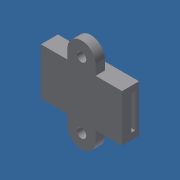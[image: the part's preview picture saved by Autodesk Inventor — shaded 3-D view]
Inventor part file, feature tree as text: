
AUTODESK INVENTOR PART (.ipt)
format: ipt  version: 2021 (Build 250183000, 183)  size: 143,360 bytes
history: native  units: mm
features: extrude x3, sketch x3
ambient origin geometry x8: Origin, YZ Plane, XZ Plane, XY Plane, X Axis, Y Axis, Z Axis, Center Point
bodies: Solid1 (feature_tree)
feature tree (6):
  extrude  "Extrusion1"  Depth=25.0mm
  extrude  "Extrusion2"  Depth=15.0mm
  extrude  "Extrusion3"  Depth=21.5mm
  sketch  "Sketch1"  dims[d0=43.0mm d1=25.0mm]
  sketch  "Sketch2"  dims[d2=15.0mm d3=15.0mm]
  sketch  "Sketch3"  dims[d4=21.5mm d5=21.5mm d6=5.0mm d7=5.0mm d8=5.0mm d9=5.0mm d10=5.0mm d11=0.0mm d12=3.5mm d13=3.5mm d14=2.0mm d15=0.0mm d16=4.0mm d17=4.0mm d18=0.0mm d19=2.0mm d20=2.0mm d21=2.0mm d22=0.0mm]
